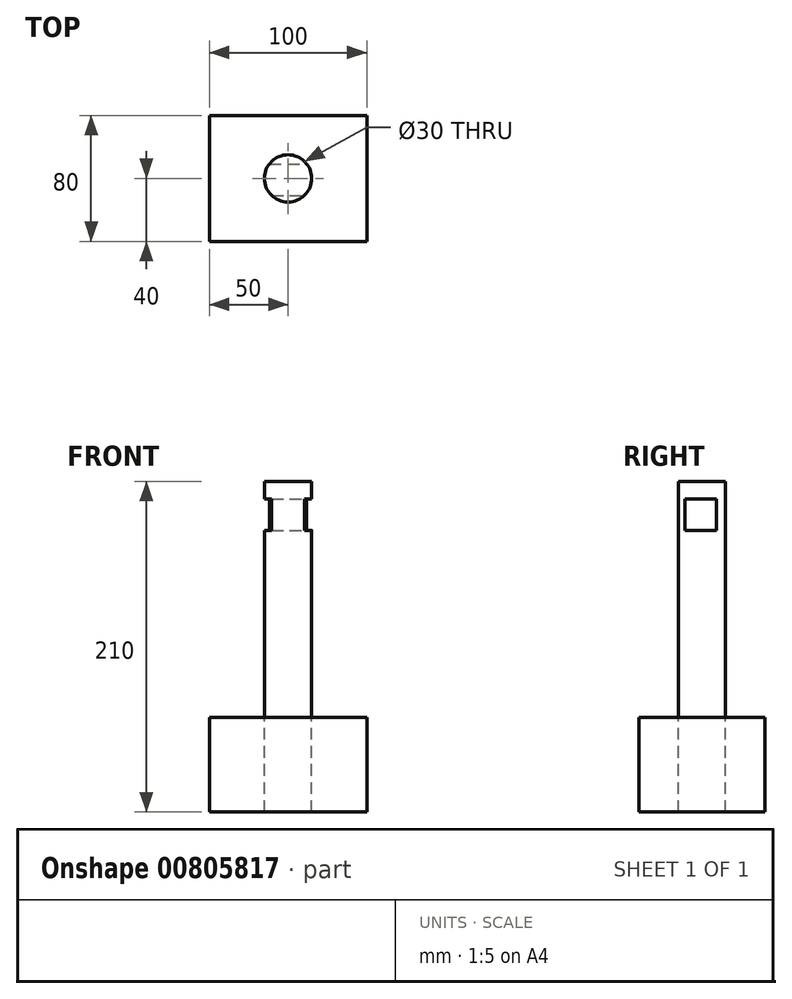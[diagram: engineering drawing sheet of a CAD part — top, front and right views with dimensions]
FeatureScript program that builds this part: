
annotation { "Feature Type Name" : "Feature", "Feature Type Description" : "" }
export const myFeature = defineFeature(function(context is Context, id is Id, definition is map)
    precondition{}
    {
        {
            var Q0;
            Q0=qCreatedBy(makeId("Top.planeOp"),FACE);
            var sketch = newSketch(context, id + "F0", { "sketchPlane" : qUnion([Q0])});
            skLineSegment(sketch, "E0.bottom", {"start": v(-50, 40) * mm, "end": v(50, 40) * mm});
            skLineSegment(sketch, "E0.top", {"start": v(-50, -40) * mm, "end": v(50, -40) * mm});
            skLineSegment(sketch, "E0.left", {"start": v(-50, 40) * mm, "end": v(-50, -40) * mm});
            skLineSegment(sketch, "E0.right", {"start": v(50, 40) * mm, "end": v(50, -40) * mm});
            skSolve(sketch);
        }
        {
            var Q0;
            Q0=makeQuery(id+"F0.imprint","IMPRINT",FACE,{"disambiguationData":[TD([[makeQuery(id+"F0.imprint","IMPRINT",EDGE,{"derivedFrom":sQuery(id+"F0.wireOp",EDGE,"E0.bottom")}),-1.0]])]});
            extrude(context, id + "F1", {"entities" : qUnion([Q0]), "depth" : 60 * mm, "offsetDistance" : 25 * mm});
        }
        {
            var Q0;
            Q0=makeQuery(id+"F1.opExtrude","CAP_FACE",FACE,{"disambiguationData":[OSD([sQuery(id+"F0.wireOp",EDGE,"E0.bottom"),sQuery(id+"F0.wireOp",EDGE,"E0.top"),sQuery(id+"F0.wireOp",EDGE,"E0.left"),sQuery(id+"F0.wireOp",EDGE,"E0.right")])],"isStart":false});
            var sketch = newSketch(context, id + "F2", { "sketchPlane" : qUnion([Q0])});
            skCircle(sketch, "E1", {"center": v(0, 0) * mm, "radius": 15 * mm});
            skSolve(sketch);
        }
        {
            var Q0;
            Q0=makeQuery(id+"F2.imprint","IMPRINT",FACE,{"disambiguationData":[TD([[makeQuery(id+"F2.imprint","IMPRINT",EDGE,{"derivedFrom":sQuery(id+"F2.wireOp",EDGE,"E1")}),1.0]])]});
            extrude(context, id + "F3", {"entities" : qUnion([Q0]), "operationType" : NewBodyOperationType.REMOVE, "endBound" : BoundingType.UP_TO_NEXT, "oppositeDirection" : true, "depth" : 25 * mm, "offsetDistance" : 25 * mm});
        }
        {
            var Q0;
            Q0=makeQuery(id+"F1.opExtrude","CAP_FACE",FACE,{"disambiguationData":[OSD([sQuery(id+"F0.wireOp",EDGE,"E0.bottom"),sQuery(id+"F0.wireOp",EDGE,"E0.top"),sQuery(id+"F0.wireOp",EDGE,"E0.left"),sQuery(id+"F0.wireOp",EDGE,"E0.right")])],"isStart":false});
            var sketch = newSketch(context, id + "F4", { "sketchPlane" : qUnion([Q0])});
            skCircle(sketch, "E2", {"center": v(0, 0) * mm, "radius": 15 * mm});
            skSolve(sketch);
        }
        {
            var Q0;
            Q0=makeQuery(id+"F4.imprint","IMPRINT",FACE,{"disambiguationData":[TD([[makeQuery(id+"F4.imprint","IMPRINT",EDGE,{"derivedFrom":sQuery(id+"F4.wireOp",EDGE,"E2")}),1.0]])]});
            extrude(context, id + "F5", {"entities" : qUnion([Q0]), "depth" : 150 * mm, "offsetDistance" : 25 * mm});
        }
        {
            var Q0;
            Q0=qCreatedBy(makeId("Right.planeOp"),FACE);
            var sketch = newSketch(context, id + "F6", { "sketchPlane" : qUnion([Q0])});
            skLineSegment(sketch, "E3.bottom", {"start": v(-10.8, 198.96) * mm, "end": v(9.2, 198.96) * mm});
            skLineSegment(sketch, "E3.top", {"start": v(-10.8, 178.96) * mm, "end": v(9.2, 178.96) * mm});
            skLineSegment(sketch, "E3.left", {"start": v(-10.8, 198.96) * mm, "end": v(-10.8, 178.96) * mm});
            skLineSegment(sketch, "E3.right", {"start": v(9.2, 198.96) * mm, "end": v(9.2, 178.96) * mm});
            skSolve(sketch);
        }
        {
            var Q0;
            Q0 = qSketchRegion(id + "F6", true);
            extrude(context, id + "F7", {"entities" : qUnion([Q0]), "operationType" : NewBodyOperationType.REMOVE, "oppositeDirection" : true, "depth" : 25 * mm, "offsetDistance" : 25 * mm, "hasSecondDirection" : true, "secondDirectionOppositeDirection" : false, "secondDirectionDepth" : 25 * mm});
        }
    });
